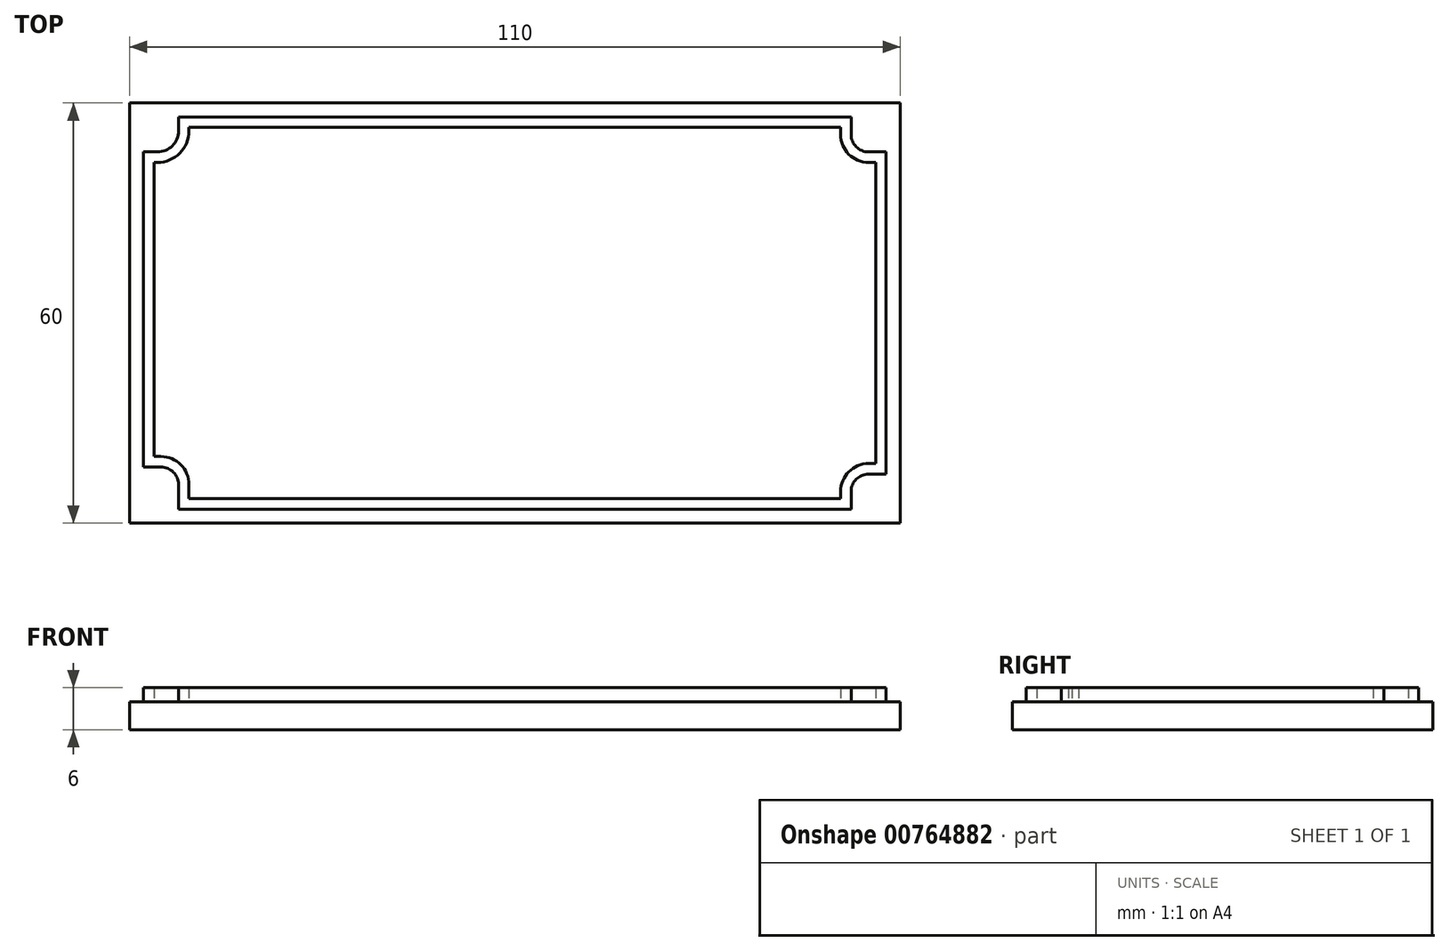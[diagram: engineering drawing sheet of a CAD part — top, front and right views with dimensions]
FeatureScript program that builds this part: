
annotation { "Feature Type Name" : "Feature", "Feature Type Description" : "" }
export const myFeature = defineFeature(function(context is Context, id is Id, definition is map)
    precondition{}
    {
        {
            var Q0;
            Q0=qCreatedBy(makeId("Top.planeOp"),FACE);
            var sketch = newSketch(context, id + "F0", { "sketchPlane" : qUnion([Q0])});
            skLineSegment(sketch, "E0.bottom", {"start": v(0, 0) * mm, "end": v(110, 0) * mm});
            skLineSegment(sketch, "E0.top", {"start": v(0, 60) * mm, "end": v(110, 60) * mm});
            skLineSegment(sketch, "E0.left", {"start": v(0, 0) * mm, "end": v(0, 60) * mm});
            skLineSegment(sketch, "E0.right", {"start": v(110, 0) * mm, "end": v(110, 60) * mm});
            skSolve(sketch);
        }
        {
            var Q0;
            Q0=makeQuery(id+"F0.imprint","IMPRINT",FACE,{"disambiguationData":[TD([[makeQuery(id+"F0.imprint","IMPRINT",EDGE,{"derivedFrom":sQuery(id+"F0.wireOp",EDGE,"E0.bottom")}),1.0]])]});
            extrude(context, id + "F1", {"entities" : qUnion([Q0]), "depth" : 4 * mm, "offsetDistance" : 25 * mm});
        }
        {
            var Q0;
            Q0=makeQuery(id+"F1.opExtrude","CAP_FACE",FACE,{"disambiguationData":[OSD([sQuery(id+"F0.wireOp",EDGE,"E0.bottom"),sQuery(id+"F0.wireOp",EDGE,"E0.top"),sQuery(id+"F0.wireOp",EDGE,"E0.left"),sQuery(id+"F0.wireOp",EDGE,"E0.right")])],"isStart":false});
            var sketch = newSketch(context, id + "F2", { "sketchPlane" : qUnion([Q0])});
            skLineSegment(sketch, "E1.0.0", {"start": v(110, 60) * mm, "end": v(0, 60) * mm});
            skLineSegment(sketch, "E1.0.1", {"start": v(0, 60) * mm, "end": v(0, 0) * mm});
            skLineSegment(sketch, "E1.0.2", {"start": v(0, 0) * mm, "end": v(110, 0) * mm});
            skLineSegment(sketch, "E1.0.3", {"start": v(110, 0) * mm, "end": v(110, 60) * mm});
            skLineSegment(sketch, "E2", {"start": v(3.5, 9.5) * mm, "end": v(3.5, 51.5) * mm});
            skLineSegment(sketch, "E3", {"start": v(3.5, 51.5) * mm, "end": v(4, 51.5) * mm});
            skLineSegment(sketch, "E4", {"start": v(8.5, 56) * mm, "end": v(8.5, 56.5) * mm});
            skLineSegment(sketch, "E5", {"start": v(8.5, 56.5) * mm, "end": v(101.5, 56.5) * mm});
            skLineSegment(sketch, "E6", {"start": v(101.5, 56.5) * mm, "end": v(101.5, 55.5) * mm});
            skLineSegment(sketch, "E7", {"start": v(105.5, 51.5) * mm, "end": v(106.5, 51.5) * mm});
            skLineSegment(sketch, "E8", {"start": v(106.5, 51.5) * mm, "end": v(106.5, 8.5) * mm});
            skLineSegment(sketch, "E9", {"start": v(106.5, 8.5) * mm, "end": v(105.5, 8.5) * mm});
            skLineSegment(sketch, "E10", {"start": v(101.5, 4.5) * mm, "end": v(101.5, 3.5) * mm});
            skLineSegment(sketch, "E11", {"start": v(101.5, 3.5) * mm, "end": v(8.5, 3.5) * mm});
            skLineSegment(sketch, "E12", {"start": v(8.5, 3.5) * mm, "end": v(8.5, 5.5) * mm});
            skLineSegment(sketch, "E13", {"start": v(4.5, 9.5) * mm, "end": v(3.5, 9.5) * mm});
            skPoint(sketch, "E14.visualSharp", {"position": v(8.5, 51.5) * mm});
            skArc(sketch, "E14.filletArc", {"start": v(4, 51.5) * mm, "mid": v(7.18, 52.82) * mm, "end": v(8.5, 56) * mm});
            skPoint(sketch, "E15.visualSharp", {"position": v(101.5, 51.5) * mm});
            skArc(sketch, "E15.filletArc", {"start": v(101.5, 55.5) * mm, "mid": v(102.67, 52.67) * mm, "end": v(105.5, 51.5) * mm});
            skPoint(sketch, "E16.visualSharp", {"position": v(101.5, 8.5) * mm});
            skArc(sketch, "E16.filletArc", {"start": v(105.5, 8.5) * mm, "mid": v(102.67, 7.33) * mm, "end": v(101.5, 4.5) * mm});
            skPoint(sketch, "E17.visualSharp", {"position": v(8.5, 9.5) * mm});
            skArc(sketch, "E17.filletArc", {"start": v(8.5, 5.5) * mm, "mid": v(7.33, 8.33) * mm, "end": v(4.5, 9.5) * mm});
            skArc(sketch, "E18.0", {"start": v(4, 53) * mm, "mid": v(6.12, 53.88) * mm, "end": v(7, 56) * mm});
            skLineSegment(sketch, "E18.1", {"start": v(2, 53) * mm, "end": v(4, 53) * mm});
            skLineSegment(sketch, "E18.2", {"start": v(2, 8) * mm, "end": v(2, 53) * mm});
            skLineSegment(sketch, "E18.3", {"start": v(4.5, 8) * mm, "end": v(2, 8) * mm});
            skArc(sketch, "E18.4", {"start": v(7, 5.5) * mm, "mid": v(6.27, 7.27) * mm, "end": v(4.5, 8) * mm});
            skLineSegment(sketch, "E18.5", {"start": v(105.5, 53) * mm, "end": v(108, 53) * mm});
            skArc(sketch, "E18.6", {"start": v(103, 55.5) * mm, "mid": v(103.73, 53.73) * mm, "end": v(105.5, 53) * mm});
            skLineSegment(sketch, "E18.7", {"start": v(103, 58) * mm, "end": v(103, 55.5) * mm});
            skLineSegment(sketch, "E18.8", {"start": v(7, 58) * mm, "end": v(103, 58) * mm});
            skLineSegment(sketch, "E18.9", {"start": v(108, 53) * mm, "end": v(108, 7) * mm});
            skLineSegment(sketch, "E18.10", {"start": v(108, 7) * mm, "end": v(105.5, 7) * mm});
            skArc(sketch, "E18.11", {"start": v(105.5, 7) * mm, "mid": v(103.73, 6.27) * mm, "end": v(103, 4.5) * mm});
            skLineSegment(sketch, "E18.12", {"start": v(103, 4.5) * mm, "end": v(103, 2) * mm});
            skLineSegment(sketch, "E18.13", {"start": v(103, 2) * mm, "end": v(7, 2) * mm});
            skLineSegment(sketch, "E18.14", {"start": v(7, 56) * mm, "end": v(7, 58) * mm});
            skLineSegment(sketch, "E18.15", {"start": v(7, 2) * mm, "end": v(7, 5.5) * mm});
            skSolve(sketch);
        }
        {
            var Q0;
            Q0=makeQuery(id+"F2.imprint","IMPRINT",FACE,{"disambiguationData":[TD([[makeQuery(id+"F2.imprint","IMPRINT",EDGE,{"derivedFrom":sQuery(id+"F2.wireOp",EDGE,"E2")}),1.0]])]});
            extrude(context, id + "F3", {"entities" : qUnion([Q0]), "operationType" : NewBodyOperationType.ADD, "depth" : 2 * mm, "offsetDistance" : 25 * mm});
        }
    });
